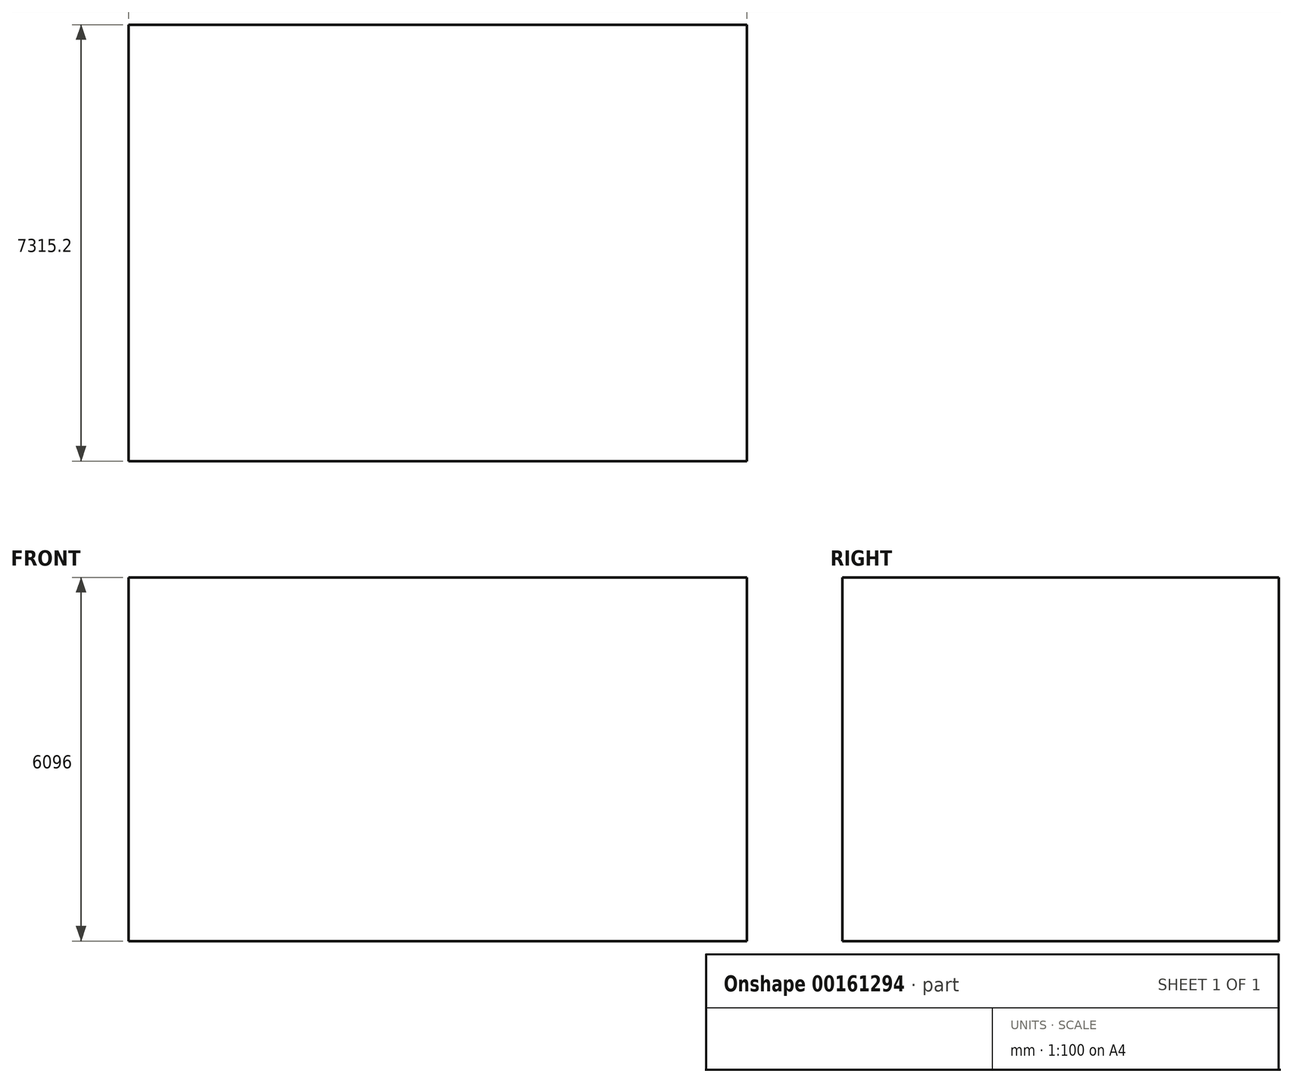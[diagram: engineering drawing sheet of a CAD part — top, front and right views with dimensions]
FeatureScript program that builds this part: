
annotation { "Feature Type Name" : "Feature", "Feature Type Description" : "" }
export const myFeature = defineFeature(function(context is Context, id is Id, definition is map)
    precondition{}
    {
        {
            var Q0;
            Q0=qCreatedBy(makeId("Top.planeOp"),FACE);
            var sketch = newSketch(context, id + "F0", { "sketchPlane" : qUnion([Q0])});
            skLineSegment(sketch, "E0.bottom", {"start": v(-5163.93, 2633.74) * mm, "end": v(5199.27, 2633.74) * mm});
            skLineSegment(sketch, "E0.top", {"start": v(-5163.93, -4681.46) * mm, "end": v(5199.27, -4681.46) * mm});
            skLineSegment(sketch, "E0.left", {"start": v(-5163.93, 2633.74) * mm, "end": v(-5163.93, -4681.46) * mm});
            skLineSegment(sketch, "E0.right", {"start": v(5199.27, 2633.74) * mm, "end": v(5199.27, -4681.46) * mm});
            skSolve(sketch);
        }
        {
            var Q0;
            Q0=makeQuery(id+"F0.imprint","IMPRINT",FACE,{"disambiguationData":[TD([[makeQuery(id+"F0.imprint","IMPRINT",EDGE,{"derivedFrom":sQuery(id+"F0.wireOp",EDGE,"E0.bottom")}),-1.0]])]});
            extrude(context, id + "F1", {"entities" : qUnion([Q0]), "depth" : 6096 * mm});
        }
    });
